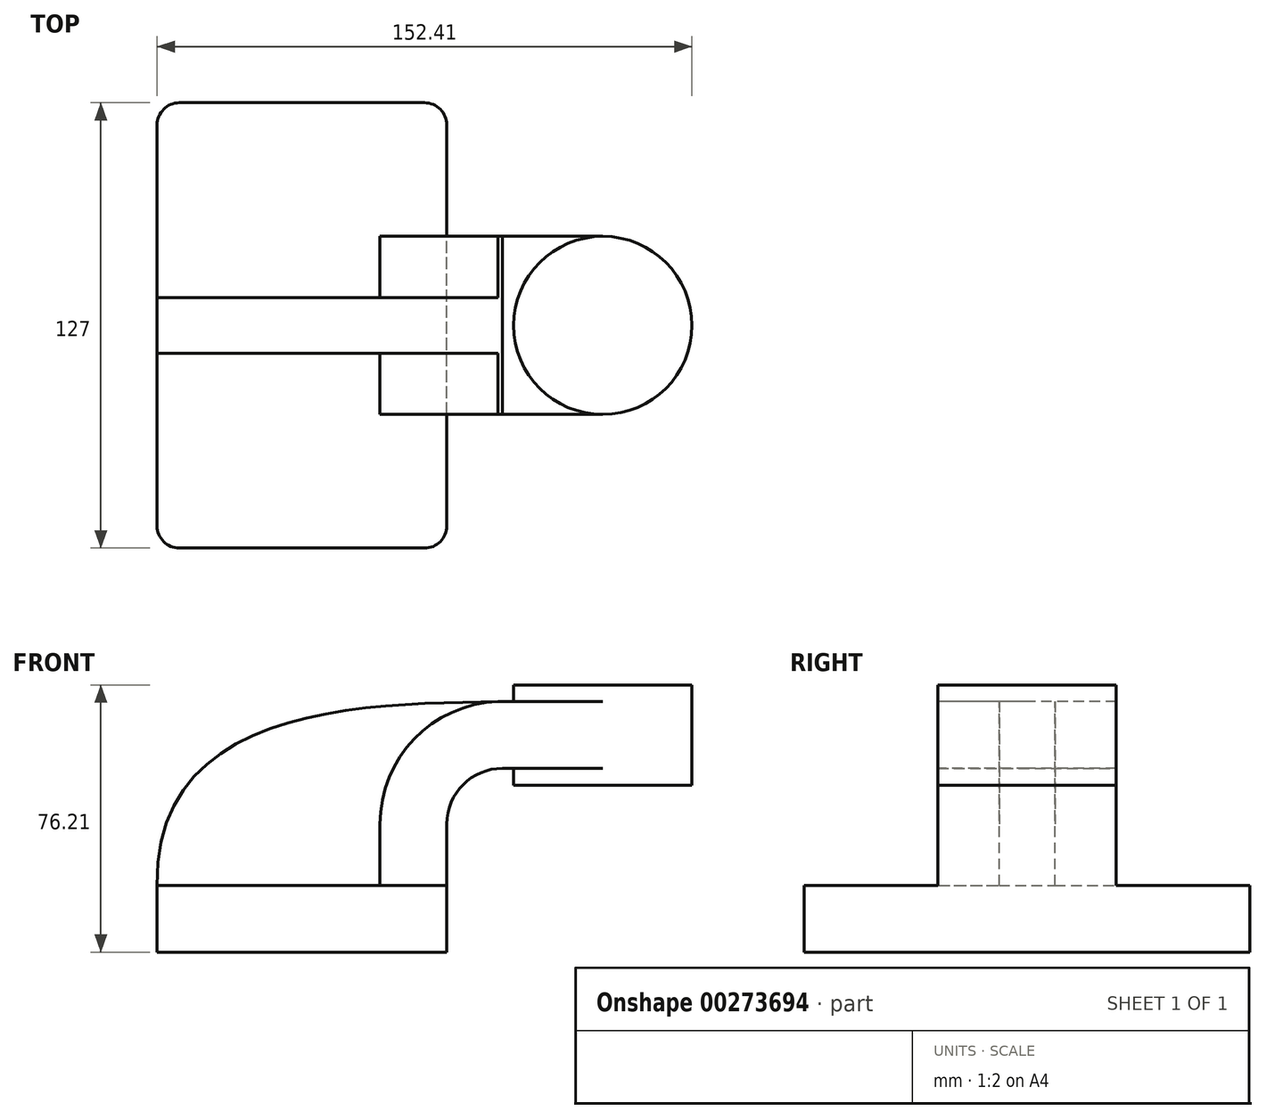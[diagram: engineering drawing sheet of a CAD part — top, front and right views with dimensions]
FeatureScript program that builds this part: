
annotation { "Feature Type Name" : "Feature", "Feature Type Description" : "" }
export const myFeature = defineFeature(function(context is Context, id is Id, definition is map)
    precondition{}
    {
        {
            var Q0;
            Q0=qCreatedBy(makeId("Front.planeOp"),FACE);
            var sketch = newSketch(context, id + "F0", { "sketchPlane" : qUnion([Q0])});
            skLineSegment(sketch, "E0.bottom", {"start": v(-41.28, 9.52) * mm, "end": v(41.27, 9.53) * mm});
            skLineSegment(sketch, "E0.top", {"start": v(-41.28, -9.53) * mm, "end": v(41.28, -9.53) * mm});
            skLineSegment(sketch, "E0.left", {"start": v(-41.28, 9.52) * mm, "end": v(-41.28, -9.53) * mm});
            skLineSegment(sketch, "E0.right", {"start": v(41.27, 9.53) * mm, "end": v(41.28, -9.52) * mm});
            skPoint(sketch, "E0.middle", {"position": v(0, 0) * mm});
            skLineSegment(sketch, "E1.bottom", {"start": v(60.32, 66.68) * mm, "end": v(111.12, 66.68) * mm});
            skLineSegment(sketch, "E1.top", {"start": v(60.32, 38.1) * mm, "end": v(111.12, 38.1) * mm});
            skLineSegment(sketch, "E1.left", {"start": v(60.32, 66.68) * mm, "end": v(60.32, 38.1) * mm});
            skLineSegment(sketch, "E1.right", {"start": v(111.12, 66.68) * mm, "end": v(111.12, 38.1) * mm});
            skPoint(sketch, "E1.middle", {"position": v(85.72, 52.39) * mm});
            skLineSegment(sketch, "E2", {"start": v(41.27, 9.53) * mm, "end": v(41.27, 27) * mm});
            skArc(sketch, "E3", {"start": v(41.27, 27) * mm, "mid": v(45.92, 38.23) * mm, "end": v(57.15, 42.88) * mm});
            skLineSegment(sketch, "E4", {"start": v(57.15, 42.88) * mm, "end": v(85.72, 42.88) * mm});
            skArc(sketch, "E5.0", {"start": v(22.22, 27) * mm, "mid": v(32.45, 51.7) * mm, "end": v(57.15, 61.93) * mm});
            skLineSegment(sketch, "E5.1", {"start": v(22.22, 9.53) * mm, "end": v(22.22, 27) * mm});
            skLineSegment(sketch, "E6.0", {"start": v(57.15, 61.93) * mm, "end": v(85.73, 61.93) * mm});
            skLineSegment(sketch, "E7", {"start": v(85.72, 38.1) * mm, "end": v(85.72, 66.68) * mm});
            skFitSpline(sketch, "E8", {"points": [v(-41.28, 9.52) * mm, v(57.15, 61.93) * mm], "startDerivative": vector(-2.4, 158.36) * mm, "endDerivative": vector(108.58, 2.08) * mm});
            skSolve(sketch);
        }
        {
            var Q0;
            Q0=makeQuery(id+"F0.imprint","IMPRINT",FACE,{"disambiguationData":[TD([[makeQuery(id+"F0.imprint","IMPRINT",EDGE,{"derivedFrom":sQuery(id+"F0.wireOp",EDGE,"E0.top")}),1.0]])]});
            extrude(context, id + "F1", {"entities" : qUnion([Q0]), "endBound" : BoundingType.SYMMETRIC, "depth" : 127 * mm});
        }
        {
            var Q0;
            {var subQ3=sQuery(id+"F0.wireOp",EDGE,"E5.1");Q0=makeQuery(id+"F0.imprint","IMPRINT",FACE,{"disambiguationData":[TD([[makeQuery(id+"F0.imprint","IMPRINT",EDGE,{"derivedFrom":subQ3}),1.0]])]});}
            extrude(context, id + "F2", {"entities" : qUnion([Q0]), "operationType" : NewBodyOperationType.ADD, "endBound" : BoundingType.SYMMETRIC, "depth" : 15.88 * mm});
        }
        {
            var Q0;
            {var subQ1=sQuery(id+"F0.wireOp",EDGE,"E2");Q0=makeQuery(id+"F0.imprint","IMPRINT",FACE,{"disambiguationData":[TD([[makeQuery(id+"F0.imprint","IMPRINT",EDGE,{"derivedFrom":subQ1}),1.0]])]});}
            var Q1;
            {var subQ0=sQuery(id+"F0.wireOp",EDGE,"E6.0");var subQ1=sQuery(id+"F0.wireOp",EDGE,"E1.left");var subQ2=makeQuery(id+"F0.imprint","INTERSECT",VERTEX,{"derivedFrom":[subQ1,subQ0]});Q1=makeQuery(id+"F0.imprint","IMPRINT",FACE,{"disambiguationData":[TD([[makeQuery(id+"F0.imprint","IMPRINT",EDGE,{"disambiguationData":[TD([[subQ2,-1.0]])],"derivedFrom":subQ1}),1.0]])]});}
            extrude(context, id + "F3", {"entities" : qUnion([Q0, Q1]), "operationType" : NewBodyOperationType.ADD, "endBound" : BoundingType.SYMMETRIC, "depth" : 50.8 * mm});
        }
        {
            var Q0;
            {var subQ0=sQuery(id+"F0.wireOp",EDGE,"E1.right");Q0=makeQuery(id+"F0.imprint","IMPRINT",FACE,{"disambiguationData":[TD([[makeQuery(id+"F0.imprint","IMPRINT",EDGE,{"derivedFrom":subQ0}),-1.0]])]});}
            var Q1;
            Q1=sQuery(id+"F0.wireOp",EDGE,"E7");
            revolve(context, id + "F4", {"operationType" : NewBodyOperationType.ADD, "entities" : qUnion([Q0]), "axis" : qUnion([Q1]), "revolveType" : RevolveType.FULL});
        }
        {
            var Q0;
            Q0=makeQuery(id+"F1.opExtrude","CAP_EDGE",EDGE,{"disambiguationData":[OSD([sQuery(id+"F0.wireOp",EDGE,"E0.right")])],"isStart":true});
            var Q1;
            Q1=makeQuery(id+"F1.opExtrude","CAP_EDGE",EDGE,{"disambiguationData":[OSD([sQuery(id+"F0.wireOp",EDGE,"E0.left")])],"isStart":true});
            var Q2;
            Q2=makeQuery(id+"F1.opExtrude","CAP_EDGE",EDGE,{"disambiguationData":[OSD([sQuery(id+"F0.wireOp",EDGE,"E0.left")])],"isStart":false});
            var Q3;
            Q3=makeQuery(id+"F1.opExtrude","CAP_EDGE",EDGE,{"disambiguationData":[OSD([sQuery(id+"F0.wireOp",EDGE,"E0.right")])],"isStart":false});
            fillet(context, id + "F5", {"entities" : qUnion([Q0, Q1, Q2, Q3]), "radius" : 6.35 * mm, "tangentPropagation" : true, "allowEdgeOverflow" : false});
        }
    });
